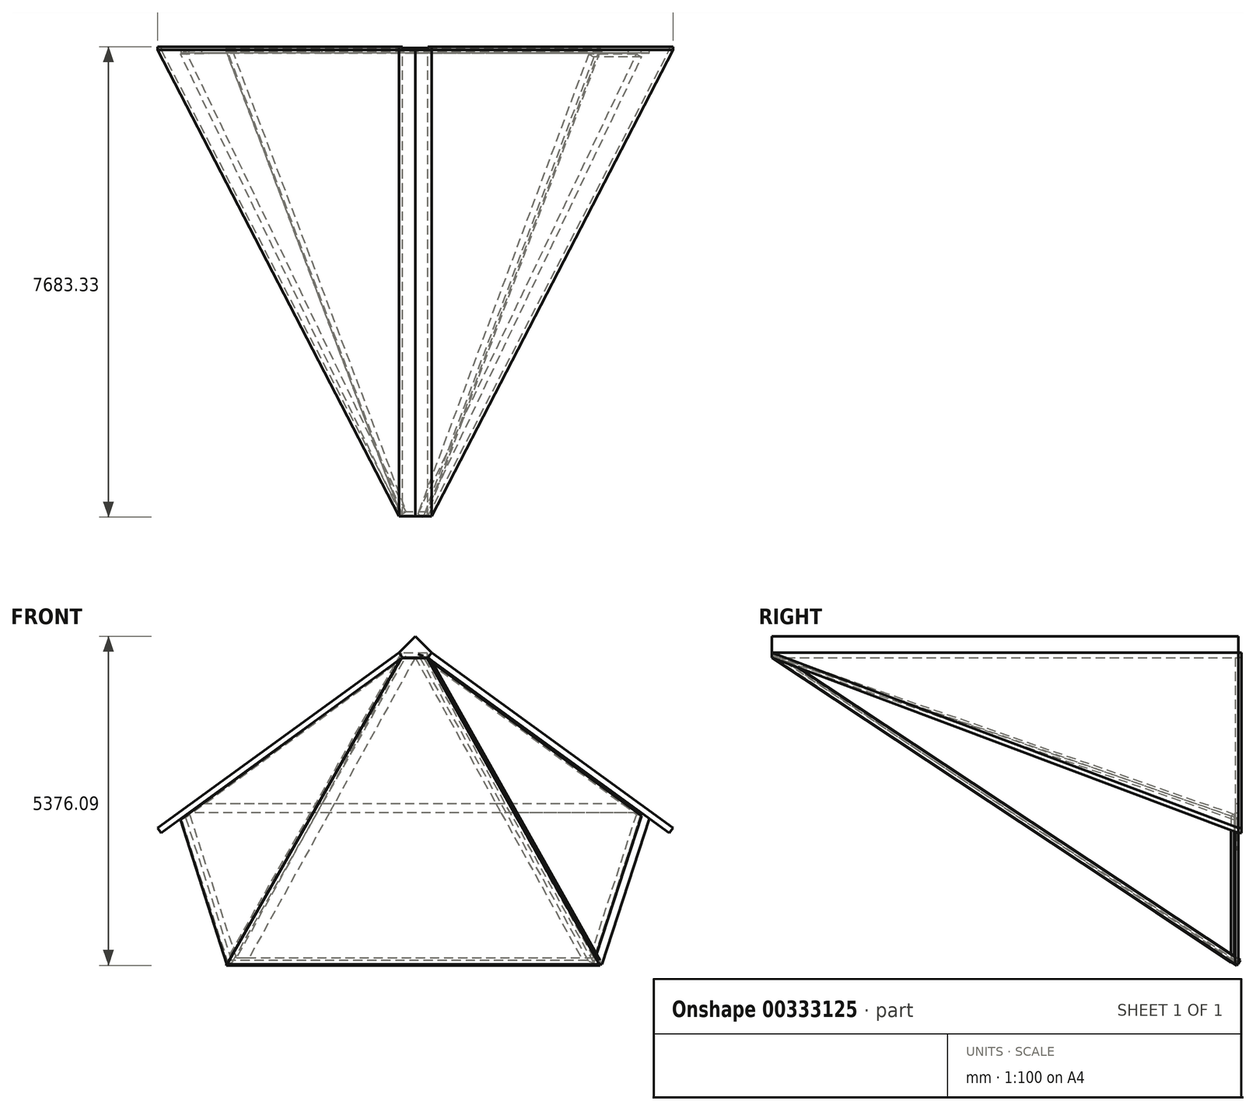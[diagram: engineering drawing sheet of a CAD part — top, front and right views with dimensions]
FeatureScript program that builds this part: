
annotation { "Feature Type Name" : "Feature", "Feature Type Description" : "" }
export const myFeature = defineFeature(function(context is Context, id is Id, definition is map)
    precondition{}
    {
        {
            var Q0;
            Q0=qCreatedBy(makeId("Front.planeOp"),FACE);
            var sketch = newSketch(context, id + "F0", { "sketchPlane" : qUnion([Q0])});
            skLineSegment(sketch, "E0", {"start": v(-164.19, -3930.32) * mm, "end": v(3781.23, -1063.8) * mm});
            skLineSegment(sketch, "E1", {"start": v(3781.23, -1063.8) * mm, "end": v(3840.95, -1146) * mm});
            skLineSegment(sketch, "E2", {"start": v(3840.95, -1146) * mm, "end": v(-104.47, -4012.51) * mm});
            skLineSegment(sketch, "E3", {"start": v(4312.49, -1063.8) * mm, "end": v(4252.77, -1146) * mm});
            skLineSegment(sketch, "E4", {"start": v(4252.77, -1146) * mm, "end": v(8198.18, -4012.51) * mm});
            skLineSegment(sketch, "E5", {"start": v(8198.18, -4012.51) * mm, "end": v(8257.9, -3930.32) * mm});
            skLineSegment(sketch, "E6", {"start": v(8257.9, -3930.32) * mm, "end": v(4312.49, -1063.8) * mm});
            skLineSegment(sketch, "E7", {"start": v(-164.19, -3930.32) * mm, "end": v(-104.47, -4012.51) * mm});
            skPoint(sketch, "E8.0.midPoint", {"position": v(4746.62, -1718.2) * mm});
            skLineSegment(sketch, "E9", {"start": v(7869.4, -3773.64) * mm, "end": v(7094.86, -6157.42) * mm});
            skLineSegment(sketch, "E10", {"start": v(7094.86, -6157.42) * mm, "end": v(998.86, -6157.42) * mm});
            skLineSegment(sketch, "E11", {"start": v(998.86, -6157.42) * mm, "end": v(224.32, -3773.64) * mm});
            skLineSegment(sketch, "E12", {"start": v(7739.76, -3679.45) * mm, "end": v(6967.63, -6055.82) * mm});
            skLineSegment(sketch, "E13", {"start": v(6967.63, -6055.82) * mm, "end": v(1126.09, -6055.82) * mm});
            skLineSegment(sketch, "E14", {"start": v(1126.09, -6055.82) * mm, "end": v(353.96, -3679.45) * mm});
            skLineSegment(sketch, "E15", {"start": v(6967.63, -6055.82) * mm, "end": v(4252.77, -1146) * mm});
            skLineSegment(sketch, "E16", {"start": v(3840.95, -1146) * mm, "end": v(1126.09, -6055.82) * mm});
            skLineSegment(sketch, "E17", {"start": v(4046.86, -1146) * mm, "end": v(4046.86, -6055.82) * mm, "construction": true});
            skLineSegment(sketch, "E18", {"start": v(7739.76, -3679.45) * mm, "end": v(353.96, -3679.45) * mm});
            skLineSegment(sketch, "E19", {"start": v(563.72, -3527.05) * mm, "end": v(7530, -3527.05) * mm});
            skLineSegment(sketch, "E20", {"start": v(4252.77, -1146) * mm, "end": v(3840.95, -1146) * mm});
            skPoint(sketch, "E21", {"position": v(4046.86, -1146) * mm});
            skLineSegment(sketch, "E22", {"start": v(4046.86, -1146) * mm, "end": v(6761.72, -6055.82) * mm});
            skLineSegment(sketch, "E23", {"start": v(4046.86, -1146) * mm, "end": v(1332, -6055.82) * mm});
            skLineSegment(sketch, "E24", {"start": v(4312.49, -1063.8) * mm, "end": v(4046.86, -798.18) * mm});
            skLineSegment(sketch, "E25", {"start": v(4046.86, -798.18) * mm, "end": v(3781.23, -1063.8) * mm});
            skLineSegment(sketch, "E26", {"start": v(4046.86, -798.18) * mm, "end": v(4046.86, -1146) * mm, "construction": true});
            skSolve(sketch);
        }
        {
            var Q0;
            {var subQ5=sQuery(id+"F0.wireOp",EDGE,"DrRXBY5q-uydS-b3ny-LOhw-fSfkwkCd4fKi");Q0=makeQuery(id+"F0.imprint","IMPRINT",FACE,{"disambiguationData":[TD([[makeQuery(id+"F0.imprint","IMPRINT",EDGE,{"derivedFrom":subQ5}),1.0]])]});}
            var Q1;
            {var subQ5=sQuery(id+"F0.wireOp",EDGE,"E0");Q1=makeQuery(id+"F0.imprint","IMPRINT",FACE,{"disambiguationData":[TD([[makeQuery(id+"F0.imprint","IMPRINT",EDGE,{"derivedFrom":subQ5}),-1.0]])]});}
            var Q2;
            {var subQ0=sQuery(id+"F0.wireOp",EDGE,"E5");Q2=makeQuery(id+"F0.imprint","IMPRINT",FACE,{"disambiguationData":[TD([[makeQuery(id+"F0.imprint","IMPRINT",EDGE,{"derivedFrom":subQ0}),1.0]])]});}
            extrude(context, id + "F1", {"entities" : qUnion([Q0, Q1, Q2]), "oppositeDirection" : true, "depth" : 50.8 * mm});
        }
        {
            var Q0;
            {var subQ4=sQuery(id+"F0.wireOp",EDGE,"E3");Q0=makeQuery(id+"F0.imprint","IMPRINT",FACE,{"disambiguationData":[TD([[makeQuery(id+"F0.imprint","IMPRINT",EDGE,{"derivedFrom":subQ4}),1.0]])]});}
            var Q1;
            Q1=makeQuery(id+"F0.imprint","IMPRINT",FACE,{"disambiguationData":[TD([[makeQuery(id+"F0.imprint","IMPRINT",EDGE,{"derivedFrom":sQuery(id+"F0.wireOp",EDGE,"E0")}),-1.0]])]});
            extrude(context, id + "F2", {"entities" : qUnion([Q0, Q1]), "depth" : 7620 * mm});
        }
        {
            var Q0;
            Q0=makeQuery(id+"F2.opExtrude","SWEPT_FACE",FACE,{"disambiguationData":[OSD([sQuery(id+"F0.wireOp",EDGE,"E6")])]});
            var sketch = newSketch(context, id + "F3", { "sketchPlane" : qUnion([Q0])});
            skLineSegment(sketch, "E27", {"start": v(4114.16, -7620) * mm, "end": v(8990.96, 0) * mm});
            skLineSegment(sketch, "E28", {"start": v(8990.96, 0) * mm, "end": v(8990.96, -7620) * mm});
            skLineSegment(sketch, "E29", {"start": v(8990.96, -7620) * mm, "end": v(4114.16, -7620) * mm});
            skSolve(sketch);
        }
        {
            var Q0;
            Q0=makeQuery(id+"F3.imprint","IMPRINT",FACE,{"disambiguationData":[TD([[makeQuery(id+"F3.imprint","IMPRINT",EDGE,{"derivedFrom":sQuery(id+"F3.wireOp",EDGE,"E27")}),-1.0]])]});
            extrude(context, id + "F4", {"entities" : qUnion([Q0]), "operationType" : NewBodyOperationType.REMOVE, "endBound" : BoundingType.THROUGH_ALL, "oppositeDirection" : true, "depth" : 25.4 * mm});
        }
        {
            var Q0;
            Q0=makeQuery(id+"F2.opExtrude","SWEPT_FACE",FACE,{"disambiguationData":[OSD([sQuery(id+"F0.wireOp",EDGE,"E0")])]});
            var sketch = newSketch(context, id + "F5", { "sketchPlane" : qUnion([Q0])});
            skLineSegment(sketch, "E30", {"start": v(2433.79, -7620) * mm, "end": v(-2443.01, 0) * mm});
            skLineSegment(sketch, "E31", {"start": v(-2443.01, 0) * mm, "end": v(-2443.01, -7620) * mm});
            skLineSegment(sketch, "E32", {"start": v(-2443.01, -7620) * mm, "end": v(2433.79, -7620) * mm});
            skSolve(sketch);
        }
        {
            var Q0;
            Q0=makeQuery(id+"F5.imprint","IMPRINT",FACE,{"disambiguationData":[TD([[makeQuery(id+"F5.imprint","IMPRINT",EDGE,{"derivedFrom":sQuery(id+"F5.wireOp",EDGE,"E30")}),1.0]])]});
            extrude(context, id + "F6", {"entities" : qUnion([Q0]), "operationType" : NewBodyOperationType.REMOVE, "endBound" : BoundingType.THROUGH_ALL, "oppositeDirection" : true, "depth" : 25.4 * mm});
        }
        {
            var Q0;
            {var subQ1=sQuery(id+"F0.wireOp",EDGE,"E15");var subQ3=sQuery(id+"F0.wireOp",EDGE,"E19");var subQ4=makeQuery(id+"F0.imprint","INTERSECT",VERTEX,{"derivedFrom":[subQ1,subQ3]});Q0=makeQuery(id+"F0.imprint","IMPRINT",FACE,{"disambiguationData":[TD([[makeQuery(id+"F0.imprint","IMPRINT",EDGE,{"disambiguationData":[TD([[subQ4,1.0]])],"derivedFrom":subQ3}),1.0]])]});}
            var Q1;
            {var subQ1=sQuery(id+"F0.wireOp",EDGE,"E16");var subQ3=sQuery(id+"F0.wireOp",EDGE,"E19");var subQ4=makeQuery(id+"F0.imprint","INTERSECT",VERTEX,{"derivedFrom":[subQ1,subQ3]});Q1=makeQuery(id+"F0.imprint","IMPRINT",FACE,{"disambiguationData":[TD([[makeQuery(id+"F0.imprint","IMPRINT",EDGE,{"disambiguationData":[TD([[subQ4,-1.0]])],"derivedFrom":subQ3}),1.0]])]});}
            extrude(context, id + "F7", {"entities" : qUnion([Q0, Q1]), "depth" : 50.8 * mm});
        }
        {
            var Q0;
            {var subQ4=sQuery(id+"F0.wireOp",EDGE,"E9");Q0=makeQuery(id+"F0.imprint","IMPRINT",FACE,{"disambiguationData":[TD([[makeQuery(id+"F0.imprint","IMPRINT",EDGE,{"derivedFrom":subQ4}),-1.0]])]});}
            extrude(context, id + "F8", {"entities" : qUnion([Q0]), "depth" : 50.8 * mm});
        }
        {
            var Q0;
            {var subQ0=sQuery(id+"F0.wireOp",EDGE,"E15");var subQ5=sQuery(id+"F0.wireOp",EDGE,"E18");var subQ6=makeQuery(id+"F0.imprint","INTERSECT",VERTEX,{"derivedFrom":[subQ0,subQ5]});Q0=makeQuery(id+"F0.imprint","IMPRINT",FACE,{"disambiguationData":[TD([[makeQuery(id+"F0.imprint","IMPRINT",EDGE,{"disambiguationData":[TD([[subQ6,-1.0]])],"derivedFrom":subQ5}),1.0]])]});}
            var Q1;
            {var subQ0=sQuery(id+"F0.wireOp",EDGE,"E18");var subQ5=sQuery(id+"F0.wireOp",EDGE,"E15");var subQ6=makeQuery(id+"F0.imprint","INTERSECT",VERTEX,{"derivedFrom":[subQ5,subQ0]});Q1=makeQuery(id+"F0.imprint","IMPRINT",FACE,{"disambiguationData":[TD([[makeQuery(id+"F0.imprint","IMPRINT",EDGE,{"disambiguationData":[TD([[subQ6,-1.0]])],"derivedFrom":subQ5}),-1.0]])]});}
            var Q2;
            {var subQ3=sQuery(id+"F0.wireOp",EDGE,"E19");var subQ5=sQuery(id+"F0.wireOp",EDGE,"E16");var subQ6=makeQuery(id+"F0.imprint","INTERSECT",VERTEX,{"derivedFrom":[subQ5,subQ3]});Q2=makeQuery(id+"F0.imprint","IMPRINT",FACE,{"disambiguationData":[TD([[makeQuery(id+"F0.imprint","IMPRINT",EDGE,{"disambiguationData":[TD([[subQ6,-1.0]])],"derivedFrom":subQ5}),-1.0]])]});}
            var Q3;
            {var subQ0=sQuery(id+"F0.wireOp",EDGE,"E16");var subQ5=sQuery(id+"F0.wireOp",EDGE,"E18");var subQ7=makeQuery(id+"F0.imprint","INTERSECT",VERTEX,{"derivedFrom":[subQ0,subQ5]});Q3=makeQuery(id+"F0.imprint","IMPRINT",FACE,{"disambiguationData":[TD([[makeQuery(id+"F0.imprint","IMPRINT",EDGE,{"disambiguationData":[TD([[subQ7,1.0]])],"derivedFrom":subQ5}),1.0]])]});}
            extrude(context, id + "F9", {"entities" : qUnion([Q0, Q1, Q2, Q3]), "depth" : 50.8 * mm});
        }
        {
            var Q0;
            {var subQ0=sQuery(id+"F0.wireOp",EDGE,"E22");var subQ1=sQuery(id+"F0.wireOp",EDGE,"E18");var subQ2=makeQuery(id+"F0.imprint","INTERSECT",VERTEX,{"derivedFrom":[subQ1,subQ0]});Q0=makeQuery(id+"F0.imprint","IMPRINT",FACE,{"disambiguationData":[TD([[makeQuery(id+"F0.imprint","IMPRINT",EDGE,{"disambiguationData":[TD([[subQ2,-1.0]])],"derivedFrom":subQ1}),-1.0]])]});}
            extrude(context, id + "F10", {"entities" : qUnion([Q0]), "depth" : 50.8 * mm});
        }
        {
            var Q0;
            Q0=makeQuery(id+"F2.opExtrude","CAP_VERTEX",VERTEX,{"disambiguationData":[OSD([sQuery(id+"F0.wireOp",EDGE,"E3"),sQuery(id+"F0.wireOp",EDGE,"E4"),sQuery(id+"F0.wireOp",EDGE,"E15"),sQuery(id+"F0.wireOp",EDGE,"E20")])],"isStart":false});
            var Q1;
            Q1=makeQuery(id+"F2.opExtrude","CAP_VERTEX",VERTEX,{"disambiguationData":[OSD([sQuery(id+"F0.wireOp",EDGE,"E1"),sQuery(id+"F0.wireOp",EDGE,"E2"),sQuery(id+"F0.wireOp",EDGE,"E16"),sQuery(id+"F0.wireOp",EDGE,"E20")])],"isStart":false});
            var Q2;
            Q2=makeQuery(id+"F8.opExtrude","CAP_VERTEX",VERTEX,{"disambiguationData":[OSD([sQuery(id+"F0.wireOp",EDGE,"E10"),sQuery(id+"F0.wireOp",EDGE,"E11")])],"isStart":false});
            cPlane(context, id + "F11", {"entities" : qUnion([Q0, Q1, Q2]), "cplaneType" : CPlaneType.THREE_POINT, "offset" : 25.4 * mm, "width" : 152.4 * mm, "height" : 152.4 * mm});
        }
        {
            var Q0;
            Q0=qCreatedBy(id+"F11.planeOp",FACE);
            var sketch = newSketch(context, id + "F12", { "sketchPlane" : qUnion([Q0])});
            skLineSegment(sketch, "E33", {"start": v(7065.02, 3387.37) * mm, "end": v(4239.75, -5703.82) * mm});
            skLineSegment(sketch, "E34", {"start": v(4239.75, -5703.82) * mm, "end": v(3817.1, -5703.82) * mm});
            skLineSegment(sketch, "E35", {"start": v(3817.1, -5703.82) * mm, "end": v(962.11, 3387.37) * mm});
            skLineSegment(sketch, "E36", {"start": v(962.11, 3387.37) * mm, "end": v(7065.02, 3387.37) * mm});
            skSolve(sketch);
        }
        {
            var Q0;
            Q0=makeQuery(id+"F12.imprint","IMPRINT",FACE,{"disambiguationData":[TD([[makeQuery(id+"F12.imprint","IMPRINT",EDGE,{"derivedFrom":sQuery(id+"F12.wireOp",EDGE,"E33")}),-1.0]])]});
            extrude(context, id + "F13", {"entities" : qUnion([Q0]), "depth" : 101.6 * mm});
        }
        {
            var Q0;
            Q0=makeQuery(id+"F13.opExtrude","CAP_EDGE",EDGE,{"disambiguationData":[OSD([sQuery(id+"F12.wireOp",EDGE,"E33")])],"isStart":false});
            var Q1;
            Q1=makeQuery(id+"F8.opExtrude","CAP_EDGE",EDGE,{"disambiguationData":[OSD([sQuery(id+"F0.wireOp",EDGE,"E9")])],"isStart":true});
            cPlane(context, id + "F14", {"entities" : qUnion([Q0, Q1]), "cplaneType" : CPlaneType.LINE_ANGLE, "offset" : 25.4 * mm, "angle" : 0 * degree, "width" : 152.4 * mm, "height" : 152.4 * mm});
        }
        {
            var Q0;
            Q0=qCreatedBy(id+"F14.planeOp",FACE);
            var sketch = newSketch(context, id + "F15", { "sketchPlane" : qUnion([Q0])});
            skLineSegment(sketch, "E37", {"start": v(-4555.59, 228.55) * mm, "end": v(4054.39, -1155.77) * mm});
            skLineSegment(sketch, "E38", {"start": v(4054.39, -1155.77) * mm, "end": v(4054.39, -3681.8) * mm});
            skLineSegment(sketch, "E39", {"start": v(4054.39, -3681.8) * mm, "end": v(-4555.59, 228.55) * mm});
            skSolve(sketch);
        }
        {
            var Q0;
            Q0=makeQuery(id+"F15.imprint","IMPRINT",FACE,{"disambiguationData":[TD([[makeQuery(id+"F15.imprint","IMPRINT",EDGE,{"derivedFrom":sQuery(id+"F15.wireOp",EDGE,"E37")}),-1.0]])]});
            extrude(context, id + "F16", {"entities" : qUnion([Q0]), "oppositeDirection" : true, "depth" : 101.6 * mm});
        }
        {
            var Q0;
            Q0=makeQuery(id+"F13.opExtrude","CAP_EDGE",EDGE,{"disambiguationData":[OSD([sQuery(id+"F12.wireOp",EDGE,"E35")])],"isStart":true});
            var Q1;
            Q1=makeQuery(id+"F8.opExtrude","CAP_EDGE",EDGE,{"disambiguationData":[OSD([sQuery(id+"F0.wireOp",EDGE,"E11")])],"isStart":false});
            cPlane(context, id + "F17", {"entities" : qUnion([Q0, Q1]), "cplaneType" : CPlaneType.LINE_ANGLE, "offset" : 25.4 * mm, "angle" : 0 * degree, "width" : 152.4 * mm, "height" : 152.4 * mm});
        }
        {
            var Q0;
            Q0=qCreatedBy(id+"F17.planeOp",FACE);
            var sketch = newSketch(context, id + "F18", { "sketchPlane" : qUnion([Q0])});
            skLineSegment(sketch, "E40", {"start": v(436.12, -6154.64) * mm, "end": v(-8228.27, -2277.94) * mm});
            skLineSegment(sketch, "E41", {"start": v(-8228.27, -2277.94) * mm, "end": v(415.34, -3674.2) * mm});
            skLineSegment(sketch, "E42", {"start": v(415.34, -3674.2) * mm, "end": v(436.12, -6154.64) * mm});
            skSolve(sketch);
        }
        {
            var Q0;
            Q0=makeQuery(id+"F18.imprint","IMPRINT",FACE,{"disambiguationData":[TD([[makeQuery(id+"F18.imprint","IMPRINT",EDGE,{"derivedFrom":sQuery(id+"F18.wireOp",EDGE,"E40")}),-1.0]])]});
            extrude(context, id + "F19", {"entities" : qUnion([Q0]), "depth" : 101.6 * mm});
        }
        {
            var Q0;
            {var subQ1=sQuery(id+"F0.wireOp",EDGE,"E1");Q0=makeQuery(id+"F0.imprint","IMPRINT",FACE,{"disambiguationData":[TD([[makeQuery(id+"F0.imprint","IMPRINT",EDGE,{"derivedFrom":subQ1}),1.0]])]});}
            extrude(context, id + "F20", {"entities" : qUnion([Q0]), "depth" : 7620 * mm});
        }
    });
